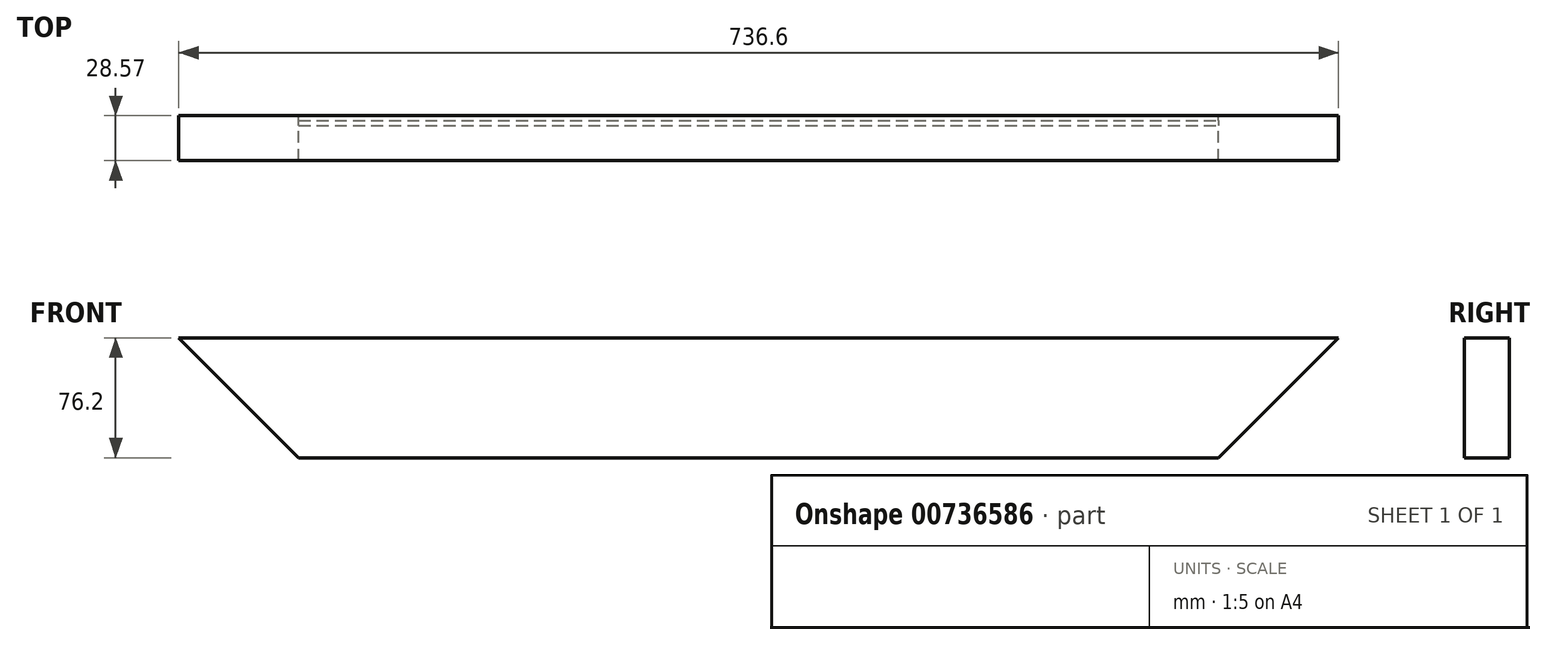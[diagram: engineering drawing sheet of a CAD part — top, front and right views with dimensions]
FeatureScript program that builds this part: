
annotation { "Feature Type Name" : "Feature", "Feature Type Description" : "" }
export const myFeature = defineFeature(function(context is Context, id is Id, definition is map)
    precondition{}
    {
        {
            var Q0;
            Q0=qCreatedBy(makeId("Front.planeOp"),FACE);
            var sketch = newSketch(context, id + "F0", { "sketchPlane" : qUnion([Q0])});
            skLineSegment(sketch, "E0.bottom", {"start": v(-595, -54.51) * mm, "end": v(-10.8, -54.51) * mm});
            skLineSegment(sketch, "E1", {"start": v(-671.2, 21.69) * mm, "end": v(-595, -54.51) * mm});
            skLineSegment(sketch, "E2", {"start": v(-10.8, -54.51) * mm, "end": v(65.4, 21.69) * mm});
            skLineSegment(sketch, "E3", {"start": v(-671.2, 21.69) * mm, "end": v(65.4, 21.69) * mm});
            skSolve(sketch);
        }
        {
            var Q0;
            Q0=makeQuery(id+"F0.imprint","IMPRINT",FACE,{"disambiguationData":[TD([[makeQuery(id+"F0.imprint","IMPRINT",EDGE,{"derivedFrom":sQuery(id+"F0.wireOp",EDGE,"E0.bottom")}),1.0]])]});
            extrude(context, id + "F1", {"entities" : qUnion([Q0]), "depth" : 28.57 * mm, "offsetDistance" : 25.4 * mm});
        }
        {
            var Q0;
            Q0=makeQuery(id+"F1.opExtrude","SWEPT_FACE",FACE,{"disambiguationData":[OSD([sQuery(id+"F0.wireOp",EDGE,"E0.bottom")])]});
            var sketch = newSketch(context, id + "F2", { "sketchPlane" : qUnion([Q0])});
            skLineSegment(sketch, "E4", {"start": v(-679, 3.18) * mm, "end": v(77.99, 3.18) * mm});
            skLineSegment(sketch, "E5", {"start": v(-679, 6.35) * mm, "end": v(77.99, 6.35) * mm});
            skLineSegment(sketch, "E6", {"start": v(-679, 3.18) * mm, "end": v(-679, 6.35) * mm});
            skLineSegment(sketch, "E7", {"start": v(77.99, 3.18) * mm, "end": v(77.99, 6.35) * mm});
            skSolve(sketch);
        }
        {
            var Q0;
            {var subQ0=sQuery(id+"F2.wireOp",EDGE,"E6");Q0=makeQuery(id+"F2.imprint","IMPRINT",FACE,{"disambiguationData":[TD([[makeQuery(id+"F2.imprint","IMPRINT",EDGE,{"derivedFrom":subQ0}),-1.0]])]});}
            var Q1;
            {var subQ0=sQuery(id+"F2.wireOp",EDGE,"E4");var subQ1=sQuery(id+"F0.wireOp",EDGE,"E0.bottom");var subQ2=makeQuery(id+"F1.opExtrude","SWEPT_EDGE",EDGE,{"disambiguationData":[OSD([subQ1,sQuery(id+"F0.wireOp",EDGE,"E1")])]});var subQ3=makeQuery(id+"F2.imprint","INTERSECT",VERTEX,{"derivedFrom":[subQ2,subQ0]});Q1=makeQuery(id+"F2.imprint","IMPRINT",FACE,{"disambiguationData":[TD([[makeQuery(id+"F2.imprint","IMPRINT",EDGE,{"disambiguationData":[TD([[subQ3,-1.0]])],"derivedFrom":subQ0}),1.0]])]});}
            var Q2;
            {var subQ0=sQuery(id+"F2.wireOp",EDGE,"E7");Q2=makeQuery(id+"F2.imprint","IMPRINT",FACE,{"disambiguationData":[TD([[makeQuery(id+"F2.imprint","IMPRINT",EDGE,{"derivedFrom":subQ0}),1.0]])]});}
            extrude(context, id + "F3", {"entities" : qUnion([Q0, Q1, Q2]), "operationType" : NewBodyOperationType.REMOVE, "oppositeDirection" : true, "depth" : 5 / 203.2 * mm, "offsetDistance" : 25.4 * mm});
        }
    });
